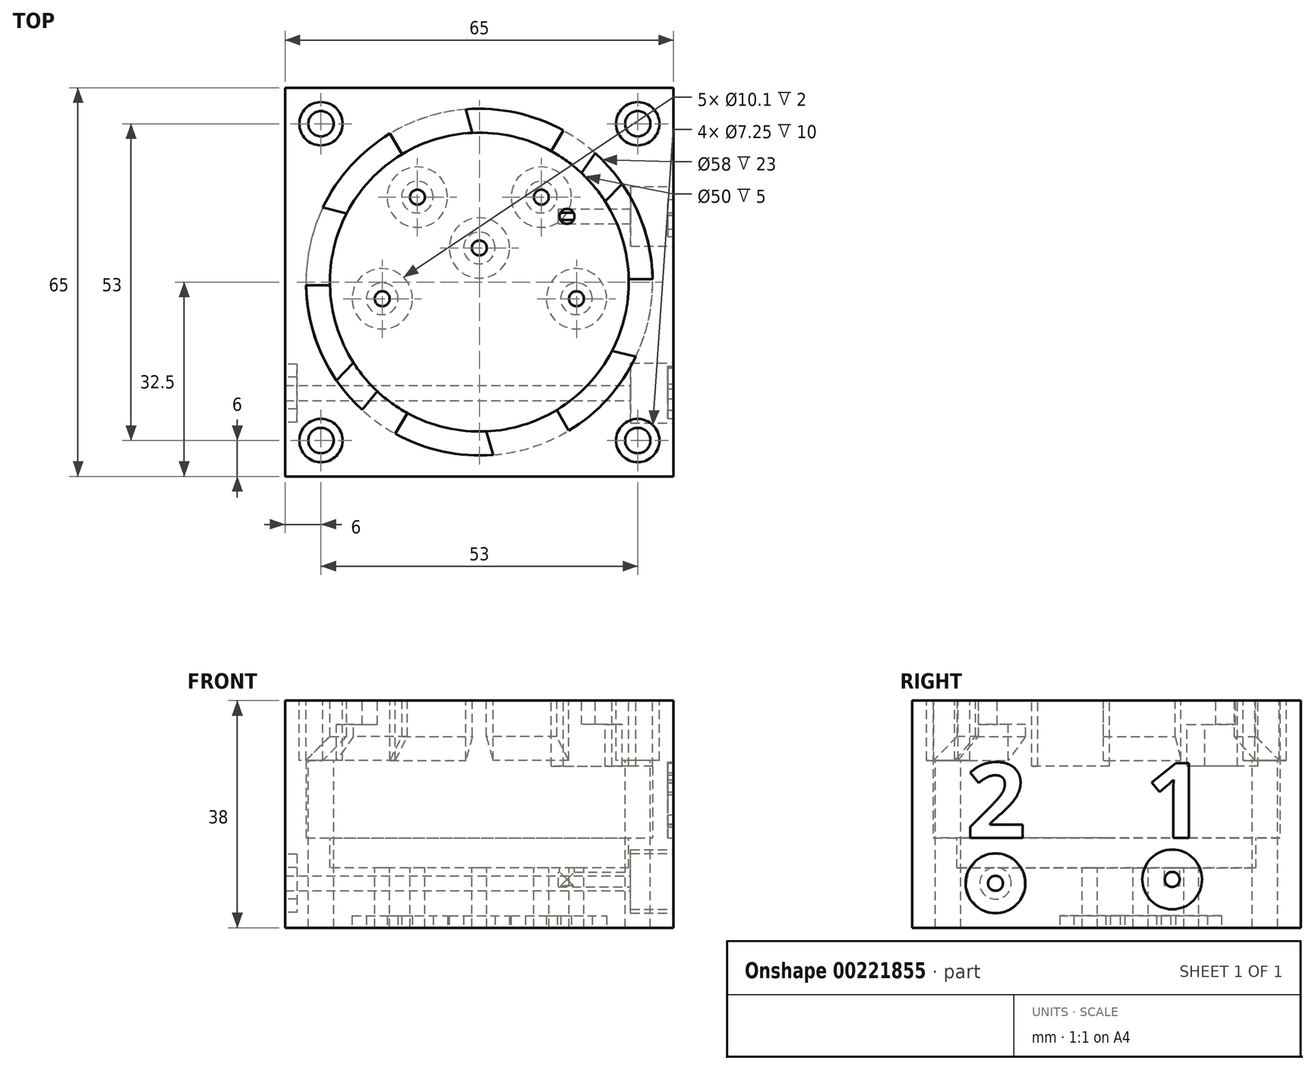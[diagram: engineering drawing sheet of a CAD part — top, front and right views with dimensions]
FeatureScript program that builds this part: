
annotation { "Feature Type Name" : "Feature", "Feature Type Description" : "" }
export const myFeature = defineFeature(function(context is Context, id is Id, definition is map)
    precondition{}
    {
        {
            var Q0;
            Q0=qCreatedBy(makeId("Top.planeOp"),FACE);
            var sketch = newSketch(context, id + "F0", { "sketchPlane" : qUnion([Q0])});
            skLineSegment(sketch, "E0.bottom", {"start": v(-32.5, 32.5) * mm, "end": v(32.5, 32.5) * mm});
            skLineSegment(sketch, "E0.top", {"start": v(-32.5, -32.5) * mm, "end": v(32.5, -32.5) * mm});
            skLineSegment(sketch, "E0.left", {"start": v(-32.5, 32.5) * mm, "end": v(-32.5, -32.5) * mm});
            skLineSegment(sketch, "E0.right", {"start": v(32.5, 32.5) * mm, "end": v(32.5, -32.5) * mm});
            skPoint(sketch, "E0.middle", {"position": v(0, 0) * mm});
            skSolve(sketch);
        }
        {
            var Q0;
            Q0=makeQuery(id+"F0.imprint","IMPRINT",FACE,{"disambiguationData":[TD([[makeQuery(id+"F0.imprint","IMPRINT",EDGE,{"derivedFrom":sQuery(id+"F0.wireOp",EDGE,"E0.bottom")}),-1.0]])]});
            extrude(context, id + "F1", {"entities" : qUnion([Q0]), "depth" : 23 * mm});
        }
        {
            var Q0;
            Q0=makeQuery(id+"F1.opExtrude","CAP_FACE",FACE,{"disambiguationData":[OSD([sQuery(id+"F0.wireOp",EDGE,"E0.bottom"),sQuery(id+"F0.wireOp",EDGE,"E0.top"),sQuery(id+"F0.wireOp",EDGE,"E0.left"),sQuery(id+"F0.wireOp",EDGE,"E0.right")])],"isStart":false});
            var sketch = newSketch(context, id + "F2", { "sketchPlane" : qUnion([Q0])});
            skCircle(sketch, "E1", {"center": v(0, 0) * mm, "radius": 29 * mm});
            skSolve(sketch);
        }
        {
            var Q0;
            Q0=makeQuery(id+"F2.imprint","IMPRINT",FACE,{"disambiguationData":[TD([[makeQuery(id+"F2.imprint","IMPRINT",EDGE,{"derivedFrom":sQuery(id+"F2.wireOp",EDGE,"E1")}),-1.0]])]});
            var sketch = newSketch(context, id + "F3", { "sketchPlane" : qUnion([Q0])});
            skCircle(sketch, "E2", {"center": v(0, 0) * mm, "radius": 25 * mm});
            skSolve(sketch);
        }
        {
            var Q0;
            Q0=makeQuery(id+"F1.opExtrude","CAP_FACE",FACE,{"disambiguationData":[OSD([sQuery(id+"F0.wireOp",EDGE,"E0.bottom"),sQuery(id+"F0.wireOp",EDGE,"E0.top"),sQuery(id+"F0.wireOp",EDGE,"E0.left"),sQuery(id+"F0.wireOp",EDGE,"E0.right")])],"isStart":true});
            var sketch = newSketch(context, id + "F4", { "sketchPlane" : qUnion([Q0])});
            skCircle(sketch, "E3", {"center": v(0, 0) * mm, "radius": 29 * mm});
            skSolve(sketch);
        }
        {
            var Q0;
            Q0=makeQuery(id+"F4.imprint","IMPRINT",FACE,{"disambiguationData":[TD([[makeQuery(id+"F4.imprint","IMPRINT",EDGE,{"derivedFrom":sQuery(id+"F4.wireOp",EDGE,"E3")}),1.0]])]});
            extrude(context, id + "F5", {"entities" : qUnion([Q0]), "operationType" : NewBodyOperationType.REMOVE, "oppositeDirection" : true, "depth" : 12 * mm});
        }
        {
            var Q0;
            Q0=makeQuery(id+"F1.opExtrude","CAP_FACE",FACE,{"disambiguationData":[OSD([sQuery(id+"F0.wireOp",EDGE,"E0.bottom"),sQuery(id+"F0.wireOp",EDGE,"E0.top"),sQuery(id+"F0.wireOp",EDGE,"E0.left"),sQuery(id+"F0.wireOp",EDGE,"E0.right")])],"isStart":true});
            var sketch = newSketch(context, id + "F6", { "sketchPlane" : qUnion([Q0])});
            skLineSegment(sketch, "E4.bottom", {"start": v(-32.5, 32.5) * mm, "end": v(32.5, 32.5) * mm});
            skLineSegment(sketch, "E4.top", {"start": v(-32.5, -32.5) * mm, "end": v(32.5, -32.5) * mm});
            skLineSegment(sketch, "E4.left", {"start": v(-32.5, 32.5) * mm, "end": v(-32.5, -32.5) * mm});
            skLineSegment(sketch, "E4.right", {"start": v(32.5, 32.5) * mm, "end": v(32.5, -32.5) * mm});
            skPoint(sketch, "E4.middle", {"position": v(0, 0) * mm});
            skSolve(sketch);
        }
        {
            var Q0;
            Q0 = qSketchRegion(id + "F6", true);
            extrude(context, id + "F7", {"entities" : qUnion([Q0]), "operationType" : NewBodyOperationType.ADD, "depth" : 15 * mm});
        }
        {
            var Q0;
            Q0=makeQuery(id+"F3.imprint","IMPRINT",FACE,{"disambiguationData":[TD([[makeQuery(id+"F3.imprint","IMPRINT",EDGE,{"derivedFrom":sQuery(id+"F3.wireOp",EDGE,"E2")}),1.0]])]});
            extrude(context, id + "F8", {"entities" : qUnion([Q0]), "operationType" : NewBodyOperationType.REMOVE, "oppositeDirection" : true, "depth" : 12 * mm});
        }
        {
            var Q0;
            Q0=makeQuery(id+"F2.imprint","IMPRINT",FACE,{"disambiguationData":[TD([[makeQuery(id+"F2.imprint","IMPRINT",EDGE,{"derivedFrom":sQuery(id+"F2.wireOp",EDGE,"E1")}),-1.0]])]});
            var sketch = newSketch(context, id + "F9", { "sketchPlane" : qUnion([Q0])});
            skPoint(sketch, "E5.center", {"position": v(0, 0) * mm});
            skCircle(sketch, "E6", {"center": v(0, 0) * mm, "radius": 25 * mm});
            skCircle(sketch, "E7", {"center": v(0, 0) * mm, "radius": 29 * mm});
            skLineSegment(sketch, "E8", {"start": v(25, 0.52) * mm, "end": v(29.09, 0.52) * mm});
            skLineSegment(sketch, "E9", {"start": v(22.2, -11.48) * mm, "end": v(26.18, -12.48) * mm});
            skLineSegment(sketch, "E10.1.0", {"start": v(12.05, 21.9) * mm, "end": v(14.1, 25.45) * mm});
            skLineSegment(sketch, "E10.1.1", {"start": v(21.05, 13.5) * mm, "end": v(23.9, 16.43) * mm});
            skLineSegment(sketch, "E10.2.0", {"start": v(-12.95, 21.39) * mm, "end": v(-15, 24.93) * mm});
            skLineSegment(sketch, "E10.2.1", {"start": v(-1.16, 24.97) * mm, "end": v(-2.28, 28.91) * mm});
            skLineSegment(sketch, "E10.3.0", {"start": v(-25, -0.52) * mm, "end": v(-29.09, -0.52) * mm});
            skLineSegment(sketch, "E10.3.1", {"start": v(-22.2, 11.48) * mm, "end": v(-26.18, 12.48) * mm});
            skLineSegment(sketch, "E10.4.0", {"start": v(-12.05, -21.9) * mm, "end": v(-14.1, -25.45) * mm});
            skLineSegment(sketch, "E10.4.1", {"start": v(-21.05, -13.5) * mm, "end": v(-23.9, -16.43) * mm});
            skLineSegment(sketch, "E10.5.0", {"start": v(12.95, -21.39) * mm, "end": v(15, -24.93) * mm});
            skLineSegment(sketch, "E10.5.1", {"start": v(1.16, -24.97) * mm, "end": v(2.28, -28.91) * mm});
            skSolve(sketch);
        }
        {
            var Q0;
            {var subQ0=sQuery(id+"F9.wireOp",EDGE,"E9");var subQ1=sQuery(id+"F9.wireOp",EDGE,"E6");var subQ2=makeQuery(id+"F9.imprint","INTERSECT",VERTEX,{"derivedFrom":[subQ1,subQ0]});Q0=makeQuery(id+"F9.imprint","IMPRINT",FACE,{"disambiguationData":[TD([[makeQuery(id+"F9.imprint","IMPRINT",EDGE,{"disambiguationData":[TD([[subQ2,1.0]])],"derivedFrom":subQ1}),-1.0]])]});}
            var Q1;
            {var subQ0=sQuery(id+"F9.wireOp",EDGE,"E10.4.0");var subQ1=sQuery(id+"F9.wireOp",EDGE,"E6");var subQ2=makeQuery(id+"F9.imprint","INTERSECT",VERTEX,{"derivedFrom":[subQ1,subQ0]});Q1=makeQuery(id+"F9.imprint","IMPRINT",FACE,{"disambiguationData":[TD([[makeQuery(id+"F9.imprint","IMPRINT",EDGE,{"disambiguationData":[TD([[subQ2,-1.0]])],"derivedFrom":subQ1}),-1.0]])]});}
            var Q2;
            {var subQ0=sQuery(id+"F9.wireOp",EDGE,"E10.3.0");var subQ1=sQuery(id+"F9.wireOp",EDGE,"E6");var subQ2=makeQuery(id+"F9.imprint","INTERSECT",VERTEX,{"derivedFrom":[subQ1,subQ0]});Q2=makeQuery(id+"F9.imprint","IMPRINT",FACE,{"disambiguationData":[TD([[makeQuery(id+"F9.imprint","IMPRINT",EDGE,{"disambiguationData":[TD([[subQ2,-1.0]])],"derivedFrom":subQ1}),-1.0]])]});}
            var Q3;
            {var subQ0=sQuery(id+"F9.wireOp",EDGE,"E10.2.0");var subQ1=sQuery(id+"F9.wireOp",EDGE,"E6");var subQ2=makeQuery(id+"F9.imprint","INTERSECT",VERTEX,{"derivedFrom":[subQ1,subQ0]});Q3=makeQuery(id+"F9.imprint","IMPRINT",FACE,{"disambiguationData":[TD([[makeQuery(id+"F9.imprint","IMPRINT",EDGE,{"disambiguationData":[TD([[subQ2,-1.0]])],"derivedFrom":subQ1}),-1.0]])]});}
            var Q4;
            {var subQ0=sQuery(id+"F9.wireOp",EDGE,"E10.1.0");var subQ1=sQuery(id+"F9.wireOp",EDGE,"E6");var subQ2=makeQuery(id+"F9.imprint","INTERSECT",VERTEX,{"derivedFrom":[subQ1,subQ0]});Q4=makeQuery(id+"F9.imprint","IMPRINT",FACE,{"disambiguationData":[TD([[makeQuery(id+"F9.imprint","IMPRINT",EDGE,{"disambiguationData":[TD([[subQ2,-1.0]])],"derivedFrom":subQ1}),-1.0]])]});}
            var Q5;
            {var subQ0=sQuery(id+"F9.wireOp",EDGE,"E8");var subQ1=sQuery(id+"F9.wireOp",EDGE,"E6");var subQ2=makeQuery(id+"F9.imprint","INTERSECT",VERTEX,{"derivedFrom":[subQ1,subQ0]});Q5=makeQuery(id+"F9.imprint","IMPRINT",FACE,{"disambiguationData":[TD([[makeQuery(id+"F9.imprint","IMPRINT",EDGE,{"disambiguationData":[TD([[subQ2,-1.0]])],"derivedFrom":subQ1}),-1.0]])]});}
            extrude(context, id + "F10", {"entities" : qUnion([Q0, Q1, Q2, Q3, Q4, Q5]), "operationType" : NewBodyOperationType.REMOVE, "oppositeDirection" : true, "depth" : 14 * mm});
        }
        {
            var Q0;
            {var subQ0=makeQuery(id+"F5.boolean.opBoolean","COPY",FACE,{"derivedFrom":makeQuery(id+"F5.opExtrude","CAP_FACE",FACE,{"disambiguationData":[OSD([sQuery(id+"F4.wireOp",EDGE,"8APgXNrs-ePPJ-dYLW-fPYc-3d3ciKKV9PCc")])],"isStart":false})});var subQ1=makeQuery(id+"F8.opExtrude","SWEPT_FACE",FACE,{"disambiguationData":[OSD([sQuery(id+"F3.wireOp",EDGE,"E2")])]});Q0=makeQuery(id+"F10.boolean.opBoolean","SPLIT",EDGE,{"disambiguationData":[TD([makeQuery(id+"F10.opExtrude","SWEPT_FACE",FACE,{"disambiguationData":[OSD([sQuery(id+"F9.wireOp",EDGE,"E10.1.0")])]})])],"derivedFrom":makeQuery(id+"F8.boolean.opBoolean","INTERSECT",EDGE,{"derivedFrom":[subQ0,subQ1]})});}
            var Q1;
            {var subQ0=makeQuery(id+"F5.boolean.opBoolean","COPY",FACE,{"derivedFrom":makeQuery(id+"F5.opExtrude","CAP_FACE",FACE,{"disambiguationData":[OSD([sQuery(id+"F4.wireOp",EDGE,"8APgXNrs-ePPJ-dYLW-fPYc-3d3ciKKV9PCc")])],"isStart":false})});var subQ1=makeQuery(id+"F8.opExtrude","SWEPT_FACE",FACE,{"disambiguationData":[OSD([sQuery(id+"F3.wireOp",EDGE,"E2")])]});Q1=makeQuery(id+"F10.boolean.opBoolean","SPLIT",EDGE,{"disambiguationData":[TD([makeQuery(id+"F10.opExtrude","SWEPT_FACE",FACE,{"disambiguationData":[OSD([sQuery(id+"F9.wireOp",EDGE,"E8")])]})])],"derivedFrom":makeQuery(id+"F8.boolean.opBoolean","INTERSECT",EDGE,{"derivedFrom":[subQ0,subQ1]})});}
            var Q2;
            {var subQ0=makeQuery(id+"F5.boolean.opBoolean","COPY",FACE,{"derivedFrom":makeQuery(id+"F5.opExtrude","CAP_FACE",FACE,{"disambiguationData":[OSD([sQuery(id+"F4.wireOp",EDGE,"E3")])],"isStart":false})});var subQ1=makeQuery(id+"F8.opExtrude","SWEPT_FACE",FACE,{"disambiguationData":[OSD([sQuery(id+"F3.wireOp",EDGE,"E2")])]});Q2=makeQuery(id+"F10.boolean.opBoolean","SPLIT",EDGE,{"disambiguationData":[TD([makeQuery(id+"F10.opExtrude","SWEPT_FACE",FACE,{"disambiguationData":[OSD([sQuery(id+"F9.wireOp",EDGE,"E10.2.0")])]})])],"derivedFrom":makeQuery(id+"F8.boolean.opBoolean","INTERSECT",EDGE,{"derivedFrom":[subQ0,subQ1]})});}
            var Q3;
            {var subQ0=makeQuery(id+"F5.boolean.opBoolean","COPY",FACE,{"derivedFrom":makeQuery(id+"F5.opExtrude","CAP_FACE",FACE,{"disambiguationData":[OSD([sQuery(id+"F4.wireOp",EDGE,"E3")])],"isStart":false})});var subQ1=makeQuery(id+"F8.opExtrude","SWEPT_FACE",FACE,{"disambiguationData":[OSD([sQuery(id+"F3.wireOp",EDGE,"E2")])]});Q3=makeQuery(id+"F10.boolean.opBoolean","SPLIT",EDGE,{"disambiguationData":[TD([makeQuery(id+"F10.opExtrude","SWEPT_FACE",FACE,{"disambiguationData":[OSD([sQuery(id+"F9.wireOp",EDGE,"E10.4.0")])]})])],"derivedFrom":makeQuery(id+"F8.boolean.opBoolean","INTERSECT",EDGE,{"derivedFrom":[subQ0,subQ1]})});}
            var Q4;
            {var subQ0=makeQuery(id+"F5.boolean.opBoolean","COPY",FACE,{"derivedFrom":makeQuery(id+"F5.opExtrude","CAP_FACE",FACE,{"disambiguationData":[OSD([sQuery(id+"F4.wireOp",EDGE,"E3")])],"isStart":false})});var subQ1=makeQuery(id+"F8.opExtrude","SWEPT_FACE",FACE,{"disambiguationData":[OSD([sQuery(id+"F3.wireOp",EDGE,"E2")])]});Q4=makeQuery(id+"F10.boolean.opBoolean","SPLIT",EDGE,{"disambiguationData":[TD([makeQuery(id+"F10.opExtrude","SWEPT_FACE",FACE,{"disambiguationData":[OSD([sQuery(id+"F9.wireOp",EDGE,"E10.3.0")])]})])],"derivedFrom":makeQuery(id+"F8.boolean.opBoolean","INTERSECT",EDGE,{"derivedFrom":[subQ0,subQ1]})});}
            var Q5;
            {var subQ0=makeQuery(id+"F5.boolean.opBoolean","COPY",FACE,{"derivedFrom":makeQuery(id+"F5.opExtrude","CAP_FACE",FACE,{"disambiguationData":[OSD([sQuery(id+"F4.wireOp",EDGE,"E3")])],"isStart":false})});var subQ1=makeQuery(id+"F8.opExtrude","SWEPT_FACE",FACE,{"disambiguationData":[OSD([sQuery(id+"F3.wireOp",EDGE,"E2")])]});Q5=makeQuery(id+"F10.boolean.opBoolean","SPLIT",EDGE,{"disambiguationData":[TD([makeQuery(id+"F10.opExtrude","SWEPT_FACE",FACE,{"disambiguationData":[OSD([sQuery(id+"F9.wireOp",EDGE,"E10.5.0")])]})])],"derivedFrom":makeQuery(id+"F8.boolean.opBoolean","INTERSECT",EDGE,{"derivedFrom":[subQ0,subQ1]})});}
            chamfer(context, id + "F11", {"entities" : qUnion([Q0, Q1, Q2, Q3, Q4, Q5]), "width" : 5 * mm, "tangentPropagation" : true});
        }
        {
            var Q0;
            Q0=makeQuery(id+"F1.opExtrude","CAP_FACE",FACE,{"disambiguationData":[OSD([sQuery(id+"F0.wireOp",EDGE,"E0.bottom"),sQuery(id+"F0.wireOp",EDGE,"E0.top"),sQuery(id+"F0.wireOp",EDGE,"E0.left"),sQuery(id+"F0.wireOp",EDGE,"E0.right")])],"isStart":false});
            var sketch = newSketch(context, id + "F12", { "sketchPlane" : qUnion([Q0])});
            skLineSegment(sketch, "E11", {"start": v(-19.6, -21.37) * mm, "end": v(-17.07, -18.26) * mm});
            skLineSegment(sketch, "E12", {"start": v(19.39, 21.57) * mm, "end": v(17.07, 18.26) * mm});
            skCircle(sketch, "E13", {"center": v(0, 0) * mm, "radius": 25 * mm});
            skCircle(sketch, "E14", {"center": v(0, 0) * mm, "radius": 29 * mm});
            skSolve(sketch);
        }
        {
            var Q0;
            {var subQ2=sQuery(id+"F12.wireOp",EDGE,"E12");Q0=makeQuery(id+"F12.imprint","IMPRINT",FACE,{"disambiguationData":[TD([[makeQuery(id+"F12.imprint","IMPRINT",EDGE,{"derivedFrom":subQ2}),1.0]])]});}
            var Q1;
            {var subQ0=sQuery(id+"F12.wireOp",EDGE,"E11");Q1=makeQuery(id+"F12.imprint","IMPRINT",FACE,{"disambiguationData":[TD([[makeQuery(id+"F12.imprint","IMPRINT",EDGE,{"derivedFrom":subQ0}),1.0]])]});}
            extrude(context, id + "F13", {"entities" : qUnion([Q0, Q1]), "operationType" : NewBodyOperationType.REMOVE, "oppositeDirection" : true, "depth" : 4 * mm});
        }
        {
            var Q0;
            Q0=makeQuery(id+"F7.boolean.opBoolean","MERGE",FACE,{"derivedFrom":[makeQuery(id+"F1.opExtrude","SWEPT_FACE",FACE,{"disambiguationData":[OSD([sQuery(id+"F0.wireOp",EDGE,"E0.right")])]}),makeQuery(id+"F7.opExtrude","SWEPT_FACE",FACE,{"disambiguationData":[OSD([sQuery(id+"F6.wireOp",EDGE,"E4.right")])]})]});
            var sketch = newSketch(context, id + "F14", { "sketchPlane" : qUnion([Q0])});
            skCircle(sketch, "E15", {"center": v(11, -6.92) * mm, "radius": 1.25 * mm});
            skSolve(sketch);
        }
        {
            var Q0;
            Q0=makeQuery(id+"F14.imprint","IMPRINT",FACE,{"disambiguationData":[TD([[makeQuery(id+"F14.imprint","IMPRINT",EDGE,{"derivedFrom":sQuery(id+"F14.wireOp",EDGE,"E15")}),1.0]])]});
            extrude(context, id + "F15", {"entities" : qUnion([Q0]), "operationType" : NewBodyOperationType.REMOVE, "oppositeDirection" : true, "depth" : 19.3 * mm});
        }
        {
            var Q0;
            Q0=makeQuery(id+"F7.boolean.opBoolean","MERGE",FACE,{"derivedFrom":[makeQuery(id+"F1.opExtrude","SWEPT_FACE",FACE,{"disambiguationData":[OSD([sQuery(id+"F0.wireOp",EDGE,"E0.right")])]}),makeQuery(id+"F7.opExtrude","SWEPT_FACE",FACE,{"disambiguationData":[OSD([sQuery(id+"F6.wireOp",EDGE,"E4.right")])]})]});
            var sketch = newSketch(context, id + "F16", { "sketchPlane" : qUnion([Q0])});
            skCircle(sketch, "E16", {"center": v(11, -6.92) * mm, "radius": 5 * mm});
            skSolve(sketch);
        }
        {
            var Q0;
            Q0=makeQuery(id+"F16.imprint","IMPRINT",FACE,{"disambiguationData":[TD([[makeQuery(id+"F16.imprint","IMPRINT",EDGE,{"derivedFrom":sQuery(id+"F16.wireOp",EDGE,"E16")}),1.0]])]});
            extrude(context, id + "F17", {"entities" : qUnion([Q0]), "operationType" : NewBodyOperationType.REMOVE, "oppositeDirection" : true, "depth" : 7.2 * mm});
        }
        {
            var Q0;
            Q0=makeQuery(id+"F7.opExtrude","CAP_FACE",FACE,{"disambiguationData":[OSD([sQuery(id+"F6.wireOp",EDGE,"E4.bottom"),sQuery(id+"F6.wireOp",EDGE,"E4.top"),sQuery(id+"F6.wireOp",EDGE,"E4.left"),sQuery(id+"F6.wireOp",EDGE,"E4.right")])],"isStart":true});
            var sketch = newSketch(context, id + "F18", { "sketchPlane" : qUnion([Q0])});
            skCircle(sketch, "E17", {"center": v(-10.37, 14.22) * mm, "radius": 1.25 * mm});
            skCircle(sketch, "E18", {"center": v(-16.25, -2.78) * mm, "radius": 1.25 * mm});
            skCircle(sketch, "E19", {"center": v(10.37, 14.22) * mm, "radius": 1.25 * mm});
            skCircle(sketch, "E20", {"center": v(16.25, -2.78) * mm, "radius": 1.25 * mm});
            skCircle(sketch, "E21", {"center": v(0, 5.72) * mm, "radius": 1.25 * mm});
            skSolve(sketch);
        }
        {
            var Q0;
            Q0=makeQuery(id+"F18.imprint","IMPRINT",FACE,{"disambiguationData":[TD([[makeQuery(id+"F18.imprint","IMPRINT",EDGE,{"derivedFrom":sQuery(id+"F18.wireOp",EDGE,"E17")}),1.0]])]});
            var Q1;
            Q1=makeQuery(id+"F18.imprint","IMPRINT",FACE,{"disambiguationData":[TD([[makeQuery(id+"F18.imprint","IMPRINT",EDGE,{"derivedFrom":sQuery(id+"F18.wireOp",EDGE,"E18")}),1.0]])]});
            var Q2;
            Q2=makeQuery(id+"F18.imprint","IMPRINT",FACE,{"disambiguationData":[TD([[makeQuery(id+"F18.imprint","IMPRINT",EDGE,{"derivedFrom":sQuery(id+"F18.wireOp",EDGE,"E21")}),1.0]])]});
            var Q3;
            Q3=makeQuery(id+"F18.imprint","IMPRINT",FACE,{"disambiguationData":[TD([[makeQuery(id+"F18.imprint","IMPRINT",EDGE,{"derivedFrom":sQuery(id+"F18.wireOp",EDGE,"E20")}),1.0]])]});
            var Q4;
            Q4=makeQuery(id+"F18.imprint","IMPRINT",FACE,{"disambiguationData":[TD([[makeQuery(id+"F18.imprint","IMPRINT",EDGE,{"derivedFrom":sQuery(id+"F18.wireOp",EDGE,"E19")}),1.0]])]});
            extrude(context, id + "F19", {"entities" : qUnion([Q0, Q1, Q2, Q3, Q4]), "operationType" : NewBodyOperationType.REMOVE, "oppositeDirection" : true, "depth" : 15 * mm});
        }
        {
            var Q0;
            Q0=makeQuery(id+"F7.opExtrude","CAP_FACE",FACE,{"disambiguationData":[OSD([sQuery(id+"F6.wireOp",EDGE,"E4.bottom"),sQuery(id+"F6.wireOp",EDGE,"E4.top"),sQuery(id+"F6.wireOp",EDGE,"E4.left"),sQuery(id+"F6.wireOp",EDGE,"E4.right")])],"isStart":false});
            var sketch = newSketch(context, id + "F20", { "sketchPlane" : qUnion([Q0])});
            skCircle(sketch, "E22", {"center": v(-10.37, -14.22) * mm, "radius": 2.65 * mm});
            skCircle(sketch, "E23", {"center": v(-10.37, -14.22) * mm, "radius": 5.05 * mm});
            skCircle(sketch, "E24", {"center": v(-16.25, 2.78) * mm, "radius": 2.65 * mm});
            skCircle(sketch, "E25", {"center": v(-16.25, 2.78) * mm, "radius": 5.05 * mm});
            skCircle(sketch, "E26", {"center": v(0, -5.72) * mm, "radius": 2.65 * mm});
            skCircle(sketch, "E27", {"center": v(0, -5.72) * mm, "radius": 5.05 * mm});
            skCircle(sketch, "E28", {"center": v(16.25, 2.78) * mm, "radius": 2.65 * mm});
            skCircle(sketch, "E29", {"center": v(16.25, 2.78) * mm, "radius": 5.05 * mm});
            skCircle(sketch, "E30", {"center": v(10.37, -14.22) * mm, "radius": 2.65 * mm});
            skCircle(sketch, "E31", {"center": v(10.37, -14.22) * mm, "radius": 5.05 * mm});
            skSolve(sketch);
        }
        {
            var Q0;
            Q0=makeQuery(id+"F1.opExtrude","CAP_FACE",FACE,{"disambiguationData":[OSD([sQuery(id+"F0.wireOp",EDGE,"E0.bottom"),sQuery(id+"F0.wireOp",EDGE,"E0.top"),sQuery(id+"F0.wireOp",EDGE,"E0.left"),sQuery(id+"F0.wireOp",EDGE,"E0.right")])],"isStart":false});
            var sketch = newSketch(context, id + "F21", { "sketchPlane" : qUnion([Q0])});
            skCircle(sketch, "E32", {"center": v(0, 0) * mm, "radius": 25 * mm});
            skSolve(sketch);
        }
        {
            var Q0;
            Q0 = qSketchRegion(id + "F21", true);
            extrude(context, id + "F22", {"entities" : qUnion([Q0]), "operationType" : NewBodyOperationType.REMOVE, "oppositeDirection" : true, "depth" : 28 * mm});
        }
        {
            var Q0;
            Q0=makeQuery(id+"F20.imprint","IMPRINT",FACE,{"disambiguationData":[TD([[makeQuery(id+"F20.imprint","IMPRINT",EDGE,{"derivedFrom":sQuery(id+"F20.wireOp",EDGE,"E22")}),-1.0]])]});
            var Q1;
            Q1=makeQuery(id+"F20.imprint","IMPRINT",FACE,{"disambiguationData":[TD([[makeQuery(id+"F20.imprint","IMPRINT",EDGE,{"derivedFrom":sQuery(id+"F20.wireOp",EDGE,"E24")}),-1.0]])]});
            var Q2;
            Q2=makeQuery(id+"F20.imprint","IMPRINT",FACE,{"disambiguationData":[TD([[makeQuery(id+"F20.imprint","IMPRINT",EDGE,{"derivedFrom":sQuery(id+"F20.wireOp",EDGE,"E26")}),-1.0]])]});
            var Q3;
            Q3=makeQuery(id+"F20.imprint","IMPRINT",FACE,{"disambiguationData":[TD([[makeQuery(id+"F20.imprint","IMPRINT",EDGE,{"derivedFrom":sQuery(id+"F20.wireOp",EDGE,"E28")}),-1.0]])]});
            var Q4;
            Q4=makeQuery(id+"F20.imprint","IMPRINT",FACE,{"disambiguationData":[TD([[makeQuery(id+"F20.imprint","IMPRINT",EDGE,{"derivedFrom":sQuery(id+"F20.wireOp",EDGE,"E30")}),-1.0]])]});
            extrude(context, id + "F23", {"entities" : qUnion([Q0, Q1, Q2, Q3, Q4]), "operationType" : NewBodyOperationType.REMOVE, "oppositeDirection" : true, "depth" : 2 * mm});
        }
        {
            var Q0;
            Q0=makeQuery(id+"F22.boolean.opBoolean","COPY",FACE,{"derivedFrom":makeQuery(id+"F22.opExtrude","CAP_FACE",FACE,{"disambiguationData":[OSD([sQuery(id+"F21.wireOp",EDGE,"E32")])],"isStart":false})});
            var sketch = newSketch(context, id + "F24", { "sketchPlane" : qUnion([Q0])});
            skCircle(sketch, "E33", {"center": v(14.67, 11) * mm, "radius": 1.25 * mm});
            skSolve(sketch);
        }
        {
            var Q0;
            Q0 = qSketchRegion(id + "F24", true);
            extrude(context, id + "F25", {"entities" : qUnion([Q0]), "operationType" : NewBodyOperationType.REMOVE, "oppositeDirection" : true, "depth" : 3 * mm});
        }
        {
            var Q0;
            Q0=makeQuery(id+"F7.boolean.opBoolean","MERGE",FACE,{"derivedFrom":[makeQuery(id+"F1.opExtrude","SWEPT_FACE",FACE,{"disambiguationData":[OSD([sQuery(id+"F0.wireOp",EDGE,"E0.right")])]}),makeQuery(id+"F7.opExtrude","SWEPT_FACE",FACE,{"disambiguationData":[OSD([sQuery(id+"F6.wireOp",EDGE,"E4.right")])]})]});
            var sketch = newSketch(context, id + "F26", { "sketchPlane" : qUnion([Q0])});
            skCircle(sketch, "E34", {"center": v(-18.56, -7.57) * mm, "radius": 1.25 * mm});
            skSolve(sketch);
        }
        {
            var Q0;
            Q0=makeQuery(id+"F26.imprint","IMPRINT",FACE,{"disambiguationData":[TD([[makeQuery(id+"F26.imprint","IMPRINT",EDGE,{"derivedFrom":sQuery(id+"F26.wireOp",EDGE,"E34")}),1.0]])]});
            extrude(context, id + "F27", {"entities" : qUnion([Q0]), "operationType" : NewBodyOperationType.REMOVE, "oppositeDirection" : true, "depth" : 65 * mm});
        }
        {
            var Q0;
            Q0=makeQuery(id+"F7.boolean.opBoolean","MERGE",FACE,{"derivedFrom":[makeQuery(id+"F1.opExtrude","SWEPT_FACE",FACE,{"disambiguationData":[OSD([sQuery(id+"F0.wireOp",EDGE,"E0.right")])]}),makeQuery(id+"F7.opExtrude","SWEPT_FACE",FACE,{"disambiguationData":[OSD([sQuery(id+"F6.wireOp",EDGE,"E4.right")])]})]});
            var sketch = newSketch(context, id + "F28", { "sketchPlane" : qUnion([Q0])});
            skCircle(sketch, "E35", {"center": v(-18.56, -7.57) * mm, "radius": 5 * mm});
            skSolve(sketch);
        }
        {
            var Q0;
            Q0=makeQuery(id+"F28.imprint","IMPRINT",FACE,{"disambiguationData":[TD([[makeQuery(id+"F28.imprint","IMPRINT",EDGE,{"derivedFrom":sQuery(id+"F28.wireOp",EDGE,"E35")}),1.0]])]});
            extrude(context, id + "F29", {"entities" : qUnion([Q0]), "operationType" : NewBodyOperationType.REMOVE, "oppositeDirection" : true, "depth" : 7.2 * mm});
        }
        {
            var Q0;
            Q0=makeQuery(id+"F7.boolean.opBoolean","MERGE",FACE,{"derivedFrom":[makeQuery(id+"F1.opExtrude","SWEPT_FACE",FACE,{"disambiguationData":[OSD([sQuery(id+"F0.wireOp",EDGE,"E0.left")])]}),makeQuery(id+"F7.opExtrude","SWEPT_FACE",FACE,{"disambiguationData":[OSD([sQuery(id+"F6.wireOp",EDGE,"E4.left")])]})]});
            var sketch = newSketch(context, id + "F30", { "sketchPlane" : qUnion([Q0])});
            skCircle(sketch, "E36", {"center": v(18.56, -7.57) * mm, "radius": 2.65 * mm});
            skCircle(sketch, "E37", {"center": v(18.56, -7.57) * mm, "radius": 4.85 * mm});
            skSolve(sketch);
        }
        {
            var Q0;
            Q0=makeQuery(id+"F30.imprint","IMPRINT",FACE,{"disambiguationData":[TD([[makeQuery(id+"F30.imprint","IMPRINT",EDGE,{"derivedFrom":sQuery(id+"F30.wireOp",EDGE,"E36")}),-1.0]])]});
            extrude(context, id + "F31", {"entities" : qUnion([Q0]), "operationType" : NewBodyOperationType.REMOVE, "oppositeDirection" : true, "depth" : 2 * mm});
        }
        {
            var Q0;
            Q0=makeQuery(id+"F1.opExtrude","CAP_FACE",FACE,{"disambiguationData":[OSD([sQuery(id+"F0.wireOp",EDGE,"E0.bottom"),sQuery(id+"F0.wireOp",EDGE,"E0.top"),sQuery(id+"F0.wireOp",EDGE,"E0.left"),sQuery(id+"F0.wireOp",EDGE,"E0.right")])],"isStart":false});
            var sketch = newSketch(context, id + "F32", { "sketchPlane" : qUnion([Q0])});
            skCircle(sketch, "E38", {"center": v(-26.5, 26.5) * mm, "radius": 3.62 * mm});
            skCircle(sketch, "E39", {"center": v(-26.5, -26.5) * mm, "radius": 3.62 * mm});
            skCircle(sketch, "E40", {"center": v(26.5, -26.5) * mm, "radius": 3.62 * mm});
            skCircle(sketch, "E41", {"center": v(26.5, 26.5) * mm, "radius": 3.62 * mm});
            skSolve(sketch);
        }
        {
            var Q0;
            Q0=makeQuery(id+"F32.imprint","IMPRINT",FACE,{"disambiguationData":[TD([[makeQuery(id+"F32.imprint","IMPRINT",EDGE,{"derivedFrom":sQuery(id+"F32.wireOp",EDGE,"E38")}),1.0]])]});
            var Q1;
            Q1=makeQuery(id+"F32.imprint","IMPRINT",FACE,{"disambiguationData":[TD([[makeQuery(id+"F32.imprint","IMPRINT",EDGE,{"derivedFrom":sQuery(id+"F32.wireOp",EDGE,"E41")}),1.0]])]});
            var Q2;
            Q2=makeQuery(id+"F32.imprint","IMPRINT",FACE,{"disambiguationData":[TD([[makeQuery(id+"F32.imprint","IMPRINT",EDGE,{"derivedFrom":sQuery(id+"F32.wireOp",EDGE,"E40")}),1.0]])]});
            var Q3;
            Q3=makeQuery(id+"F32.imprint","IMPRINT",FACE,{"disambiguationData":[TD([[makeQuery(id+"F32.imprint","IMPRINT",EDGE,{"derivedFrom":sQuery(id+"F32.wireOp",EDGE,"E39")}),1.0]])]});
            extrude(context, id + "F33", {"entities" : qUnion([Q0, Q1, Q2, Q3]), "operationType" : NewBodyOperationType.REMOVE, "oppositeDirection" : true, "depth" : 10 * mm});
        }
        {
            var Q0;
            Q0=makeQuery(id+"F7.boolean.opBoolean","MERGE",FACE,{"derivedFrom":[makeQuery(id+"F1.opExtrude","SWEPT_FACE",FACE,{"disambiguationData":[OSD([sQuery(id+"F0.wireOp",EDGE,"E0.right")])]}),makeQuery(id+"F7.opExtrude","SWEPT_FACE",FACE,{"disambiguationData":[OSD([sQuery(id+"F6.wireOp",EDGE,"E4.right")])]})]});
            var sketch = newSketch(context, id + "F34", { "sketchPlane" : qUnion([Q0])});
            skText(sketch, "E42", { "text": "1", "fontName": "OpenSans-Bold.ttf"});
            skText(sketch, "E43", { "text": "2", "fontName": "OpenSans-Bold.ttf"});
            const initialGuessF34  = {"E42": [0.00655, 0, 1, 0, 0.01265], "E43": [-0.02349, 0, 1, 0, 0.01265]};
            skSetInitialGuess(sketch, initialGuessF34);
            skSolve(sketch);
        }
        {
            var Q0;
            Q0 = qSketchRegion(id + "F34", true);
            extrude(context, id + "F35", {"entities" : qUnion([Q0]), "operationType" : NewBodyOperationType.REMOVE, "oppositeDirection" : true, "depth" : 1 * mm});
        }
        {
            var Q0;
            Q0=makeQuery(id+"F1.opExtrude","CAP_FACE",FACE,{"disambiguationData":[OSD([sQuery(id+"F0.wireOp",EDGE,"E0.bottom"),sQuery(id+"F0.wireOp",EDGE,"E0.top"),sQuery(id+"F0.wireOp",EDGE,"E0.left"),sQuery(id+"F0.wireOp",EDGE,"E0.right")])],"isStart":false});
            var sketch = newSketch(context, id + "F36", { "sketchPlane" : qUnion([Q0])});
            skCircle(sketch, "E44", {"center": v(-26.5, 26.5) * mm, "radius": 2.12 * mm});
            skCircle(sketch, "E45", {"center": v(26.5, 26.5) * mm, "radius": 2.12 * mm});
            skCircle(sketch, "E46", {"center": v(26.5, -26.5) * mm, "radius": 2.12 * mm});
            skCircle(sketch, "E47", {"center": v(-26.5, -26.5) * mm, "radius": 2.12 * mm});
            skSolve(sketch);
        }
        {
            var Q0;
            Q0 = qSketchRegion(id + "F36", true);
            extrude(context, id + "F37", {"entities" : qUnion([Q0]), "operationType" : NewBodyOperationType.REMOVE, "oppositeDirection" : true, "depth" : 39 * mm});
        }
    });
